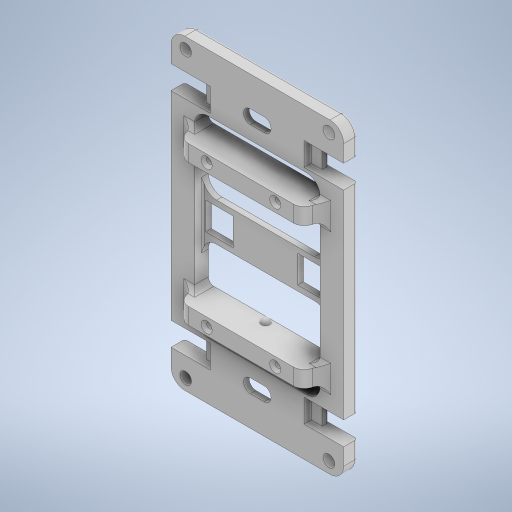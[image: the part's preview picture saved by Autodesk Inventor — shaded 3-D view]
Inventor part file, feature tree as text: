
AUTODESK INVENTOR PART (.ipt)
format: ipt  version: 2023 (Build 270158000, 158)  size: 606,720 bytes
history: native  units: mm
features: extrude x11, sketch x10, fillet x9, other x3, mirror x3, chamfer x1, revolve x1, projected_geometry x1
ambient origin geometry x8: Origin, YZ Plane, XZ Plane, XY Plane, X Axis, Y Axis, Z Axis, Center Point
bodies: Body1 (feature_tree)
feature tree (39):
  other  "솔리드1"
  extrude  "돌출1"  Depth=63.1mm
  extrude  "돌출2"  Depth=112.2mm
  extrude  "돌출3"  Depth=45.85mm
  fillet  "모깎기1"  Radius=70.23mm
  sketch  "스케치4"
  extrude  "돌출4"  Depth=5.0mm TaperAngle=0.0deg
  extrude  "돌출5"  Depth=5.0mm
  mirror  "미러1"
  mirror  "미러2"
  extrude  "돌출6"  Depth=5.0mm
  fillet  "모깎기2"  Radius=5.0mm
  mirror  "미러3"
  fillet  "모깎기3"  Radius=10.0mm
  extrude  "돌출7"  Depth=104.0mm
  fillet  "모깎기4"  Radius=4.2mm
  fillet  "모깎기5"  Radius=52.4mm
  other  "작업 평면1"
  sketch  "스케치9"
  extrude  "돌출8"  TaperAngle=0.0deg  [1 undecoded]
  extrude  "돌출9"  Depth=5.0mm
  fillet  "모깎기7"  Radius=7.0mm
  fillet  "모깎기8"  Radius=8.5mm
  chamfer  "모따기1"  Distance=3.4mm
  other  "작업 평면2"
  revolve  "회전1"
  extrude  "돌출10"  Depth=11.2mm
  fillet  "모깎기9"  Radius=4.0mm
  fillet  "모깎기10"  [1 undecoded]
  extrude  "돌출11"  Depth=2.5mm TaperAngle=0.0deg
  sketch  "스케치1"
  sketch  "스케치2"
  sketch  "스케치3"
  sketch  "스케치6"
  projected_geometry  "투영된 루프1"
  sketch  "스케치8"
  sketch  "스케치11"
  sketch  "스케치13"
  sketch  "스케치14"
note: 2 required parameter values undecoded (feature->parameter linkage not recoverable at this tier; creation-order binding heuristic only, values carry confidence <= 0.55)
